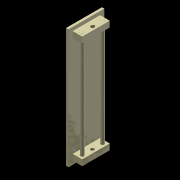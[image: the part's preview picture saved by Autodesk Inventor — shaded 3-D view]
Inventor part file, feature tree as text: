
AUTODESK INVENTOR PART (.ipt)
format: ipt  version: 2020 (Build 240168000, 168)  size: 165,376 bytes
history: native  units: mm
features: extrude x6, projected_geometry x2, other x1, thread x1, plane x1, mirror x1
ambient origin geometry x8: Origin, YZ Plane, XZ Plane, XY Plane, X Axis, Y Axis, Z Axis, Center Point
bodies: Body1 (feature_tree)
feature tree (12):
  other  "實體1"
  extrude  "Extrusion1"  Depth=3.0mm
  extrude  "Extrusion11"  Depth=6.0mm
  thread  "Thread2"  [1 undecoded]
  plane  "Work Plane3"
  extrude  "Extrusion13"  Depth=12.0mm
  mirror  "Mirror2"
  extrude  "Extrusion14"  Depth=1.0mm
  extrude  "Extrusion15"  Depth=2.0mm TaperAngle=0.0deg
  extrude  "Extrusion16"  Depth=10.0mm TaperAngle=0.0deg
  projected_geometry  "Projected Loop6"
  projected_geometry  "Projected Loop7"
note: 1 required parameter value undecoded (feature->parameter linkage not recoverable at this tier; creation-order binding heuristic only, values carry confidence <= 0.55)
